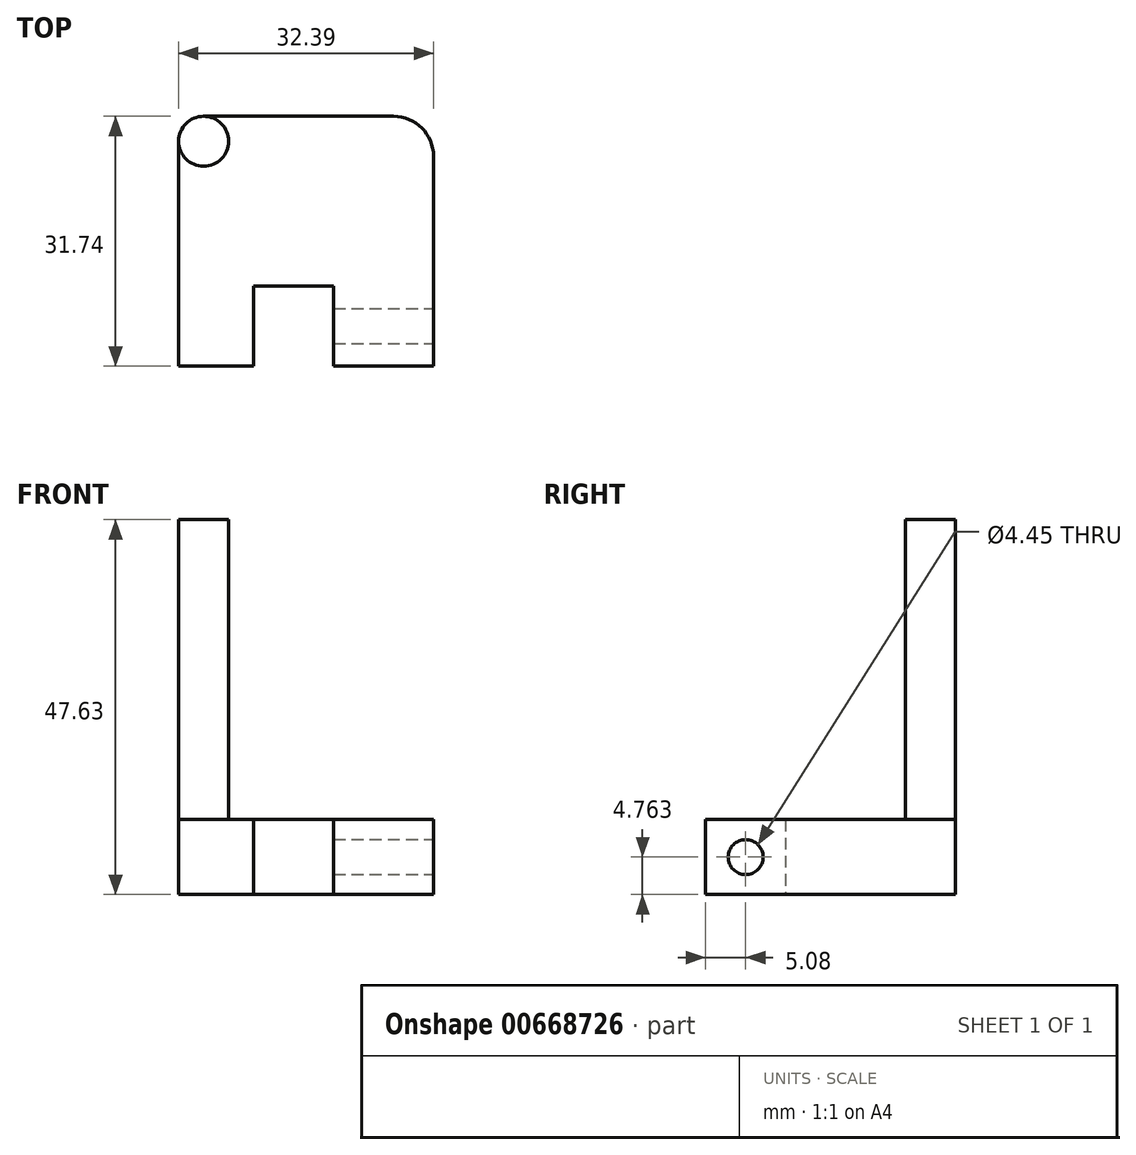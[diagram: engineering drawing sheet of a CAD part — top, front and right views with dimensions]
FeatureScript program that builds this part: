
annotation { "Feature Type Name" : "Feature", "Feature Type Description" : "" }
export const myFeature = defineFeature(function(context is Context, id is Id, definition is map)
    precondition{}
    {
        {
            var Q0;
            Q0=qCreatedBy(makeId("Top.planeOp"),FACE);
            var sketch = newSketch(context, id + "F0", { "sketchPlane" : qUnion([Q0])});
            skLineSegment(sketch, "E0.bottom", {"start": v(-10.16, -6.35) * mm, "end": v(0, -6.35) * mm});
            skLineSegment(sketch, "E0.right", {"start": v(12.7, -6.35) * mm, "end": v(12.7, 15.23) * mm});
            skPoint(sketch, "E0.middle", {"position": v(0, 0) * mm});
            skLineSegment(sketch, "E1", {"start": v(-10.16, -16.51) * mm, "end": v(-10.16, -6.35) * mm});
            skLineSegment(sketch, "E2", {"start": v(12.7, -6.35) * mm, "end": v(12.7, -16.51) * mm});
            skLineSegment(sketch, "E3", {"start": v(12.7, -16.51) * mm, "end": v(0, -16.51) * mm});
            skLineSegment(sketch, "E4", {"start": v(0, -16.51) * mm, "end": v(0, -6.35) * mm});
            skLineSegment(sketch, "E5", {"start": v(-10.16, -16.51) * mm, "end": v(-16.5, -16.51) * mm});
            skLineSegment(sketch, "E6", {"start": v(-16.51, 15.23) * mm, "end": v(12.7, 15.23) * mm});
            skArc(sketch, "E7", {"start": v(-16.51, 15.23) * mm, "mid": v(-19.69, 12.06) * mm, "end": v(-16.51, 8.88) * mm});
            skLineSegment(sketch, "E8", {"start": v(-16.51, 8.88) * mm, "end": v(-16.5, -16.51) * mm});
            skLineSegment(sketch, "E9", {"start": v(-16.5, -16.51) * mm, "end": v(-19.68, -16.51) * mm});
            skLineSegment(sketch, "E10", {"start": v(-19.68, -16.51) * mm, "end": v(-19.69, 15.23) * mm});
            skLineSegment(sketch, "E11", {"start": v(-19.69, 15.23) * mm, "end": v(-16.51, 15.23) * mm});
            skSolve(sketch);
        }
        {
            var Q0;
            Q0=makeQuery(id+"F0.imprint","IMPRINT",FACE,{"disambiguationData":[TD([[makeQuery(id+"F0.imprint","IMPRINT",EDGE,{"derivedFrom":sQuery(id+"F0.wireOp",EDGE,"E0.bottom")}),1.0]])]});
            extrude(context, id + "F1", {"entities" : qUnion([Q0]), "depth" : 9.52 * mm, "offsetDistance" : 25.4 * mm});
        }
        {
            var Q0;
            Q0=makeQuery(id+"F1.opExtrude","CAP_FACE",FACE,{"disambiguationData":[OSD([sQuery(id+"F0.wireOp",EDGE,"E0.bottom"),sQuery(id+"F0.wireOp",EDGE,"E0.right"),sQuery(id+"F0.wireOp",EDGE,"E1"),sQuery(id+"F0.wireOp",EDGE,"E2"),sQuery(id+"F0.wireOp",EDGE,"E3"),sQuery(id+"F0.wireOp",EDGE,"E4"),sQuery(id+"F0.wireOp",EDGE,"E5"),sQuery(id+"F0.wireOp",EDGE,"E6"),sQuery(id+"F0.wireOp",EDGE,"E7"),sQuery(id+"F0.wireOp",EDGE,"E8")])],"isStart":false});
            var sketch = newSketch(context, id + "F2", { "sketchPlane" : qUnion([Q0])});
            skCircle(sketch, "E12", {"center": v(-16.51, 12.06) * mm, "radius": 3.18 * mm});
            skSolve(sketch);
        }
        {
            var Q0;
            {var subQ0=sQuery(id+"F2.wireOp",EDGE,"E12");var subQ1=makeQuery(id+"F2.imprint","INTERSECT",VERTEX,{"derivedFrom":[makeQuery(id+"F1.opExtrude","CAP_EDGE",EDGE,{"disambiguationData":[OSD([sQuery(id+"F0.wireOp",EDGE,"E6")])],"isStart":false}),subQ0]});Q0=makeQuery(id+"F2.imprint","IMPRINT",FACE,{"disambiguationData":[TD([[makeQuery(id+"F2.imprint","IMPRINT",EDGE,{"disambiguationData":[TD([[subQ1,-1.0]])],"derivedFrom":subQ0}),1.0]])]});}
            extrude(context, id + "F3", {"entities" : qUnion([Q0]), "operationType" : NewBodyOperationType.ADD, "depth" : 38.1 * mm, "offsetDistance" : 25.4 * mm});
        }
        {
            var Q0;
            Q0=makeQuery(id+"F1.opExtrude","SWEPT_FACE",FACE,{"disambiguationData":[OSD([sQuery(id+"F0.wireOp",EDGE,"E2")])]});
            var sketch = newSketch(context, id + "F4", { "sketchPlane" : qUnion([Q0])});
            skCircle(sketch, "E13", {"center": v(-11.43, 4.76) * mm, "radius": 2.22 * mm});
            skPoint(sketch, "E14.orphan", {"position": v(-16.51, 9.53) * mm});
            skPoint(sketch, "E15.end.orphan", {"position": v(15.23, 0) * mm});
            skLineSegment(sketch, "E16", {"start": v(-11.43, 9.53) * mm, "end": v(-11.43, 0) * mm, "construction": true});
            skSolve(sketch);
        }
        {
            var Q0;
            Q0=makeQuery(id+"F4.imprint","IMPRINT",FACE,{"disambiguationData":[TD([[makeQuery(id+"F4.imprint","IMPRINT",EDGE,{"derivedFrom":sQuery(id+"F4.wireOp",EDGE,"E13")}),1.0]])]});
            var Q1;
            Q1=makeQuery(id+"F1.opExtrude","SWEPT_FACE",FACE,{"disambiguationData":[OSD([sQuery(id+"F0.wireOp",EDGE,"E4")])]});
            extrude(context, id + "F5", {"entities" : qUnion([Q0]), "operationType" : NewBodyOperationType.REMOVE, "endBound" : BoundingType.UP_TO_SURFACE, "oppositeDirection" : true, "depth" : 25.4 * mm, "endBoundEntityFace" : qUnion([Q1]), "offsetDistance" : 25.4 * mm});
        }
        {
            var Q0;
            Q0=makeQuery(id+"F1.opExtrude","SWEPT_EDGE",EDGE,{"disambiguationData":[OSD([sQuery(id+"F0.wireOp",EDGE,"E0.right"),sQuery(id+"F0.wireOp",EDGE,"E6")])]});
            fillet(context, id + "F6", {"entities" : qUnion([Q0]), "radius" : 5.08 * mm, "tangentPropagation" : true, "allowEdgeOverflow" : false});
        }
        {
            var Q0;
            {var subQ0=sQuery(id+"F0.wireOp",EDGE,"E8");Q0=makeQuery(id+"F0.imprint","IMPRINT",FACE,{"disambiguationData":[TD([[makeQuery(id+"F0.imprint","IMPRINT",EDGE,{"derivedFrom":subQ0}),-1.0]])]});}
            extrude(context, id + "F7", {"entities" : qUnion([Q0]), "operationType" : NewBodyOperationType.ADD, "depth" : 9.52 * mm, "offsetDistance" : 25.4 * mm});
        }
    });
